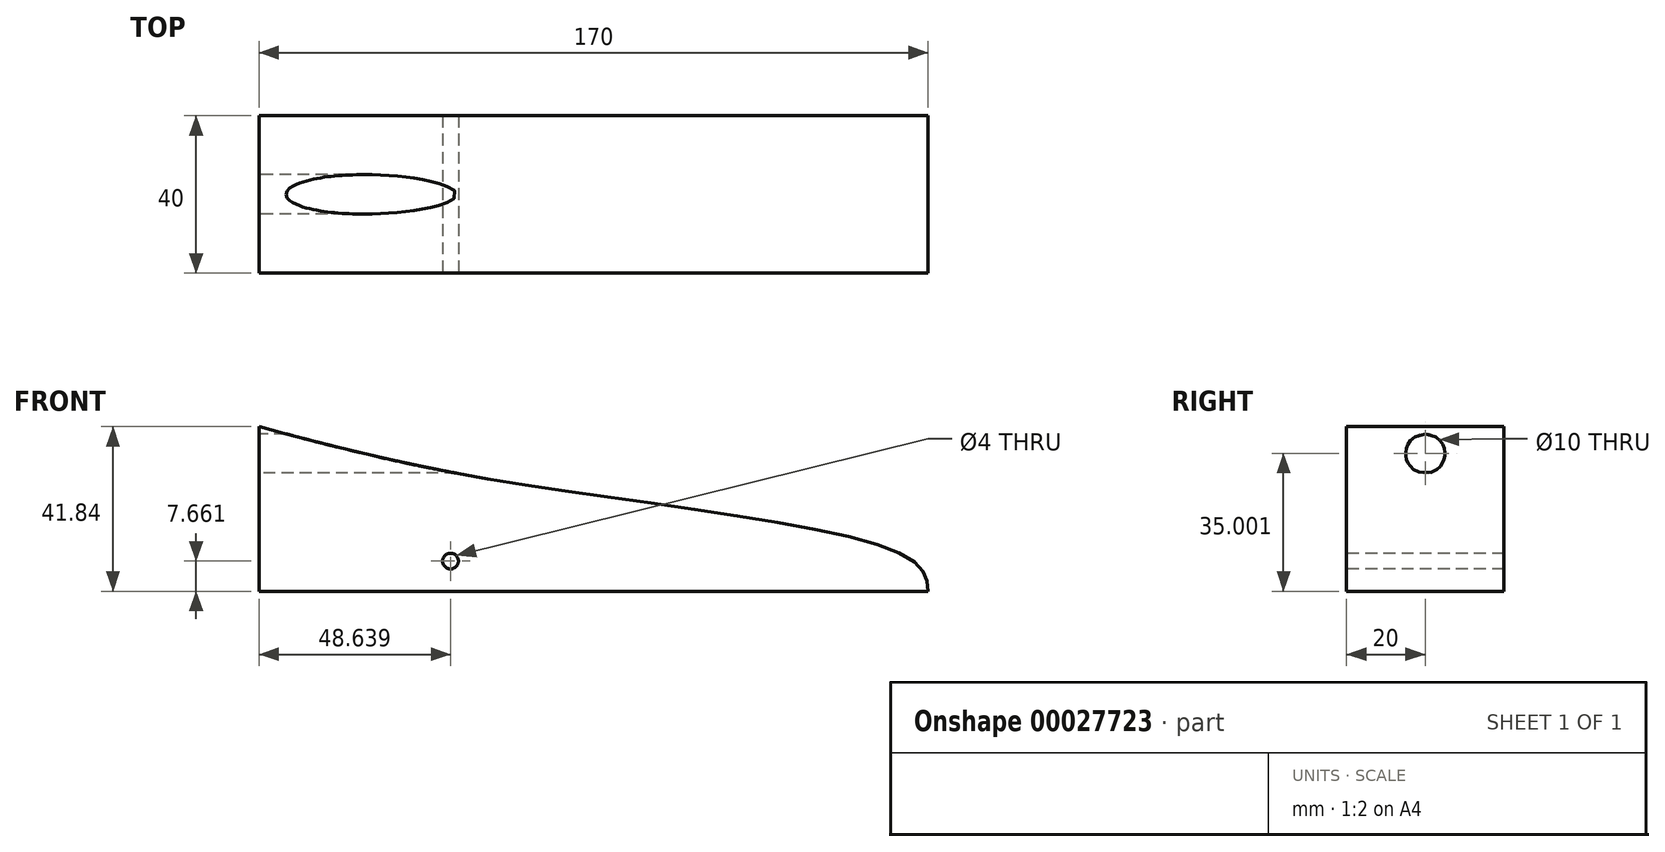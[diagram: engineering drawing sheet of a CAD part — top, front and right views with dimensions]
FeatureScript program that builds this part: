
annotation { "Feature Type Name" : "Feature", "Feature Type Description" : "" }
export const myFeature = defineFeature(function(context is Context, id is Id, definition is map)
    precondition{}
    {
        {
            var Q0;
            Q0=qCreatedBy(makeId("Front.planeOp"),FACE);
            var sketch = newSketch(context, id + "F0", { "sketchPlane" : qUnion([Q0])});
            skLineSegment(sketch, "E0.bottom", {"start": v(-84.2, -32.3) * mm, "end": v(85.8, -32.3) * mm});
            skLineSegment(sketch, "E0.top", {"start": v(-84.2, 37.7) * mm, "end": v(85.8, 37.7) * mm});
            skLineSegment(sketch, "E0.left", {"start": v(-84.2, -32.3) * mm, "end": v(-84.2, 37.7) * mm});
            skLineSegment(sketch, "E0.right", {"start": v(85.8, -32.3) * mm, "end": v(85.8, 37.7) * mm});
            skFitSpline(sketch, "E1", {"points": [v(85.8, -32.3) * mm, v(81.44, -24.15) * mm, v(-17.76, -5.12) * mm, v(-84.2, 9.54) * mm], "startDerivative": vector(-5.85, 59.3) * mm, "endDerivative": vector(-144.72, 38.93) * mm});
            skSolve(sketch);
        }
        {
            var Q0;
            Q0=makeQuery(id+"F0.imprint","IMPRINT",FACE,{"disambiguationData":[TD([[makeQuery(id+"F0.imprint","IMPRINT",EDGE,{"derivedFrom":sQuery(id+"F0.wireOp",EDGE,"E0.bottom")}),1.0]])]});
            extrude(context, id + "F1", {"entities" : qUnion([Q0]), "depth" : 40 * mm});
        }
        {
            var Q0;
            Q0=makeQuery(id+"F1.opExtrude","SWEPT_FACE",FACE,{"disambiguationData":[OSD([sQuery(id+"F0.wireOp",EDGE,"E0.left")])]});
            var sketch = newSketch(context, id + "F2", { "sketchPlane" : qUnion([Q0])});
            skCircle(sketch, "E2", {"center": v(20, 2.7) * mm, "radius": 5 * mm});
            skSolve(sketch);
        }
        {
            var Q0;
            Q0=makeQuery(id+"F2.imprint","IMPRINT",FACE,{"disambiguationData":[TD([[makeQuery(id+"F2.imprint","IMPRINT",EDGE,{"derivedFrom":sQuery(id+"F2.wireOp",EDGE,"E2")}),1.0]])]});
            extrude(context, id + "F3", {"entities" : qUnion([Q0]), "operationType" : NewBodyOperationType.REMOVE, "oppositeDirection" : true, "depth" : 65 * mm});
        }
        {
            var Q0;
            Q0=makeQuery(id+"F1.opExtrude","CAP_FACE",FACE,{"disambiguationData":[OSD([sQuery(id+"F0.wireOp",EDGE,"E0.bottom"),sQuery(id+"F0.wireOp",EDGE,"E0.top"),sQuery(id+"F0.wireOp",EDGE,"E0.left"),sQuery(id+"F0.wireOp",EDGE,"E0.right")])],"isStart":false});
            var sketch = newSketch(context, id + "F4", { "sketchPlane" : qUnion([Q0])});
            skCircle(sketch, "E3", {"center": v(-35.56, -24.64) * mm, "radius": 2 * mm});
            skCircle(sketch, "E4", {"center": v(174.33, -24.64) * mm, "radius": 2 * mm});
            skSolve(sketch);
        }
        {
            var Q0;
            Q0=makeQuery(id+"F4.imprint","IMPRINT",FACE,{"disambiguationData":[TD([[makeQuery(id+"F4.imprint","IMPRINT",EDGE,{"derivedFrom":sQuery(id+"F4.wireOp",EDGE,"E3")}),1.0]])]});
            var Q1;
            Q1=makeQuery(id+"F4.imprint","IMPRINT",FACE,{"disambiguationData":[TD([[makeQuery(id+"F4.imprint","IMPRINT",EDGE,{"derivedFrom":sQuery(id+"F4.wireOp",EDGE,"E4")}),1.0]])]});
            extrude(context, id + "F5", {"entities" : qUnion([Q0, Q1]), "operationType" : NewBodyOperationType.REMOVE, "endBound" : BoundingType.THROUGH_ALL, "oppositeDirection" : true, "depth" : 25 * mm});
        }
    });
